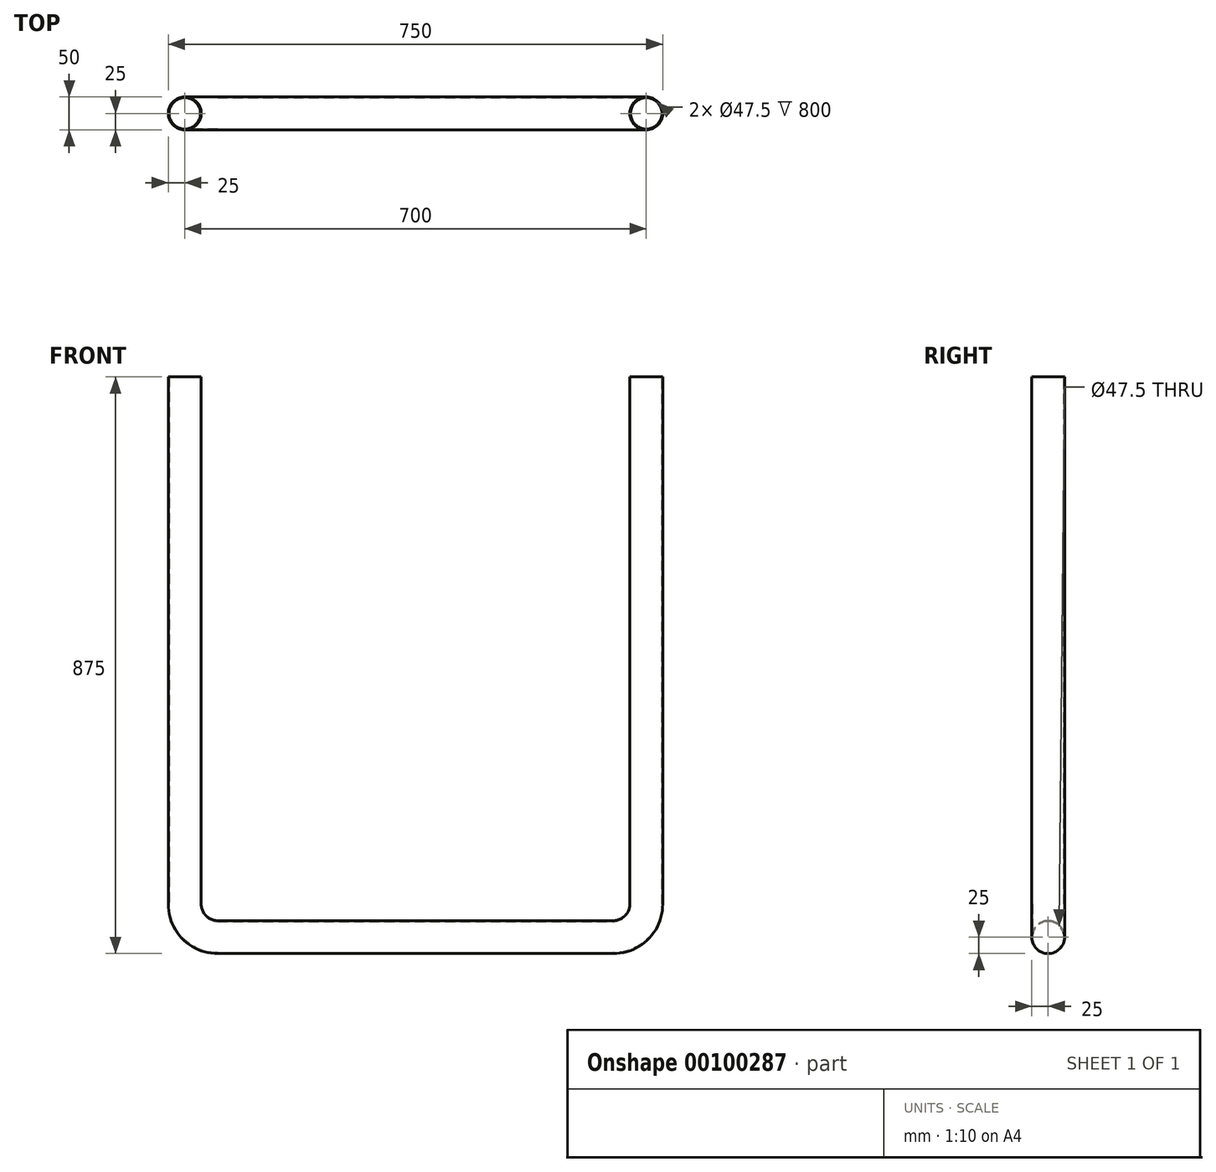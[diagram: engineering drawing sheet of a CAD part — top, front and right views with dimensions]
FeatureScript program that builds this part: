
annotation { "Feature Type Name" : "Feature", "Feature Type Description" : "" }
export const myFeature = defineFeature(function(context is Context, id is Id, definition is map)
    precondition{}
    {
        {
            var Q0;
            Q0=qCreatedBy(makeId("Front.planeOp"),FACE);
            var sketch = newSketch(context, id + "F0", { "sketchPlane" : qUnion([Q0])});
            skLineSegment(sketch, "E0", {"start": v(0, 0) * mm, "end": v(0, -800) * mm});
            skLineSegment(sketch, "E1", {"start": v(50, -850) * mm, "end": v(650, -850) * mm});
            skLineSegment(sketch, "E2", {"start": v(700, -800) * mm, "end": v(700, 0) * mm});
            skPoint(sketch, "E3.visualSharp", {"position": v(0, -850) * mm});
            skArc(sketch, "E3.filletArc", {"start": v(0, -800) * mm, "mid": v(14.64, -835.36) * mm, "end": v(50, -850) * mm});
            skPoint(sketch, "E4.visualSharp", {"position": v(700, -850) * mm});
            skArc(sketch, "E4.filletArc", {"start": v(650, -850) * mm, "mid": v(685.36, -835.36) * mm, "end": v(700, -800) * mm});
            skLineSegment(sketch, "E5", {"start": v(-692.3, 0) * mm, "end": v(623.02, 0) * mm, "construction": true});
            skSolve(sketch);
        }
        {
            var Q0;
            Q0=qCreatedBy(makeId("Top.planeOp"),FACE);
            var sketch = newSketch(context, id + "F1", { "sketchPlane" : qUnion([Q0])});
            skCircle(sketch, "E6", {"center": v(0, 0) * mm, "radius": 25 * mm});
            skCircle(sketch, "E7", {"center": v(0, 0) * mm, "radius": 23.75 * mm});
            skSolve(sketch);
        }
        {
            var Q0;
            Q0=makeQuery(id+"F1.imprint","IMPRINT",FACE,{"disambiguationData":[TD([[makeQuery(id+"F1.imprint","IMPRINT",EDGE,{"derivedFrom":sQuery(id+"F1.wireOp",EDGE,"E6")}),1.0]])]});
            var Q1;
            Q1=sQuery(id+"F0.wireOp",EDGE,"E0");
            var Q2;
            Q2=sQuery(id+"F0.wireOp",EDGE,"E3.filletArc");
            var Q3;
            Q3=sQuery(id+"F0.wireOp",EDGE,"E1");
            var Q4;
            Q4=sQuery(id+"F0.wireOp",EDGE,"E4.filletArc");
            var Q5;
            Q5=sQuery(id+"F0.wireOp",EDGE,"E2");
            sweep(context, id + "F2", {"profiles" : qUnion([Q0]), "path" : qUnion([Q1, Q2, Q3, Q4, Q5])});
        }
    });
